# Revit family: Cambio Wall Systems - Acoustic - Felt Board 18x18
name_source: partatom
category: Generic Models
units: mm (PartAtom-declared; Revit-internal decimal feet)

## family parameters
Can host rebar = No
Cut with Voids When Loaded = No
Host = Face
Maintain Annotation Orientation = No
Part Type = Normal
Room Calculation Point = No
Round Connector Dimension = Use Diameter
Shared = No

## types (35) — shared parameters
Default Elevation = 4' - 0"

## per-type parameters (varying)
| type | Cambio Material |
| Felt Board Color - BERRY | Cambio Felt Board - Berry |
| Felt Board Color - BLACK | Cambio Felt Board - Black |
| Felt Board Color - BLUE JEAN | Cambio Felt Board - Blue Jean |
| Felt Board Color - BROWN | Cambio Felt Board - Brown |
| Felt Board Color - CHARCOAL | Cambio Felt Board - Charcoal |
| Felt Board Color - EARTH BROWN | Cambio Felt Board - Earth Brown |
| Felt Board Color - GREEN | Cambio Felt Board - Green |
| Felt Board Color - GREY | Cambio Felt Board - Grey |
| Felt Board Color - HEATHER GREEN | Cambio Felt Board - Heather Green |
| Felt Board Color - HICKORY | Cambio Felt Board - Hickory |
| Felt Board Color - HONEY DEW | Cambio Felt Board - Honey Dew |
| Felt Board Color - LEMON | Cambio Felt Board - Lemon |
| Felt Board Color - LILAC | Cambio Felt Board - Lilac |
| Felt Board Color - LIME | Cambio Felt Board - Lime |
| Felt Board Color - MARBLE | Cambio Felt Board - Marble |
| Felt Board Color - MAROON | Cambio Felt Board - Maroon |
| Felt Board Color - MIDNIGHT BLUE | Cambio Felt Board - Midnight Blue |
| Felt Board Color - NAVY | Cambio Felt Board - Navy |
| Felt Board Color - OAT | Cambio Felt Board - Oat |
| Felt Board Color - ORANGE | Cambio Felt Board - Orange |
| Felt Board Color - PEAR | Cambio Felt Board - Pear |
| Felt Board Color - PEPPER | Cambio Felt Board - Pepper |
| Felt Board Color - PERIWINKLE | Cambio Felt Board - Periwinkle |
| Felt Board Color - PINK | Cambio Felt Board - Pink |
| Felt Board Color - PUMPKIN | Cambio Felt Board - Pumpkin |
| Felt Board Color - PURPLE | Cambio Felt Board - Purple |
| Felt Board Color - RED | Cambio Felt Board - Red |
| Felt Board Color - SALMON | Cambio Felt Board - Salmon |
| Felt Board Color - SAND DOLLAR | Cambio Felt Board - Sand Dollar |
| Felt Board Color - SKY BLUE | Cambio Felt Board - Sky Blue |
| Felt Board Color - STONE | Cambio Felt Board - Stone |
| Felt Board Color - TEAL | Cambio Felt Board - Teal |
| Felt Board Color - VIOLET | Cambio Felt Board - Violet |
| Felt Board Color - WHITE | Cambio Felt Board - White |
| Felt Board Color - YELLOW | Cambio Felt Board - Yellow |

## geometry (parser evidence)
native form markers: Sweep x1
no freeform markers — native parametric forms only
